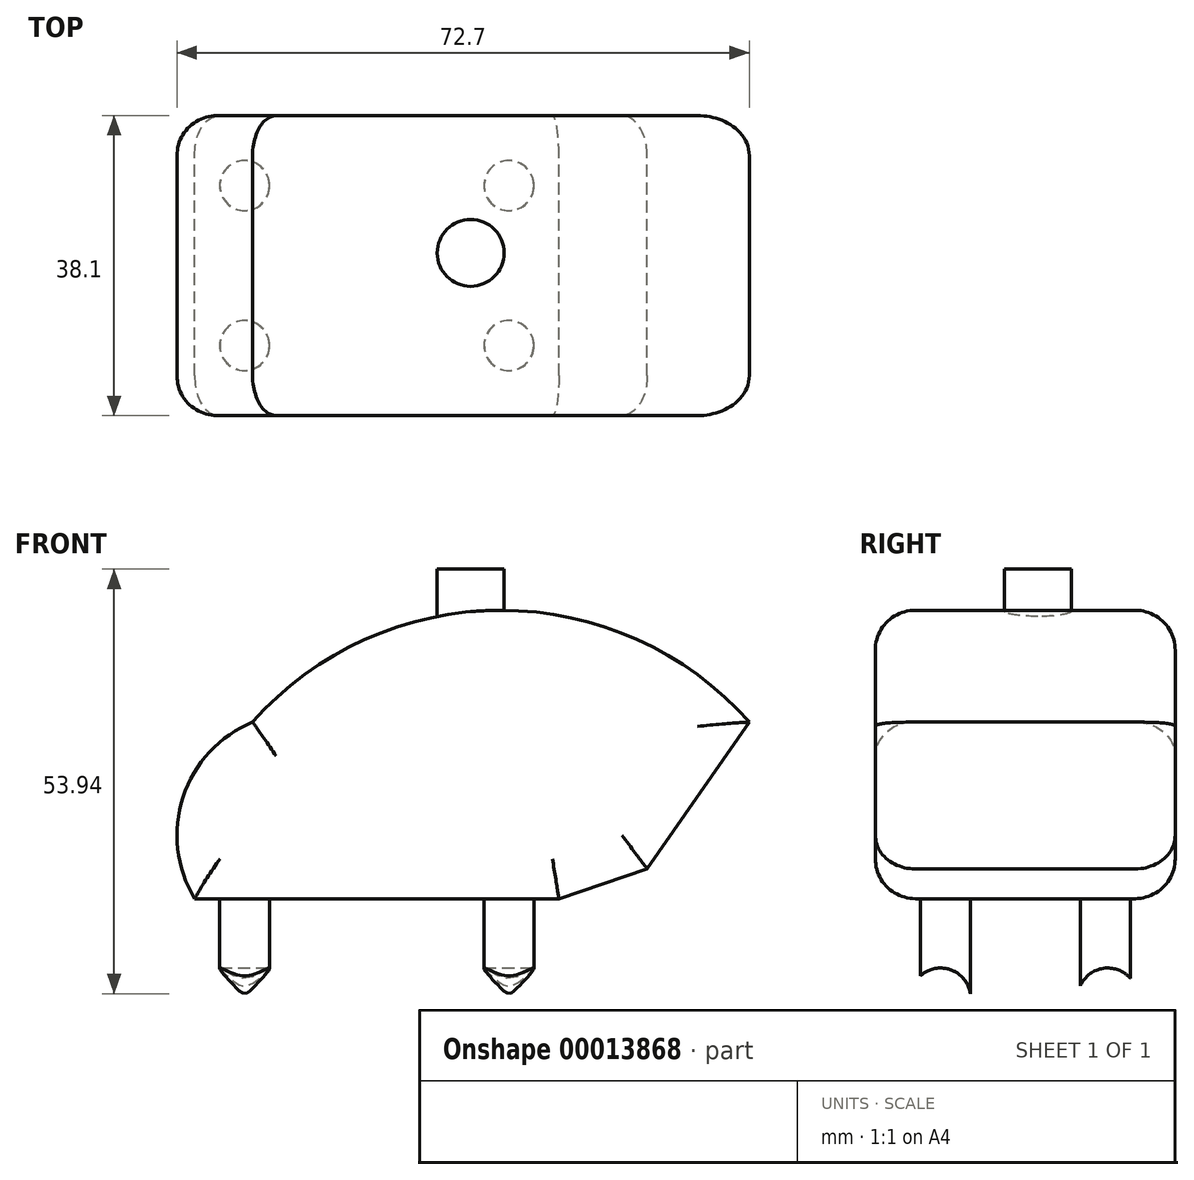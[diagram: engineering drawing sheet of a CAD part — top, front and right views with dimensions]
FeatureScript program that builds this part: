
annotation { "Feature Type Name" : "Feature", "Feature Type Description" : "" }
export const myFeature = defineFeature(function(context is Context, id is Id, definition is map)
    precondition{}
    {
        {
            var Q0;
            Q0=qCreatedBy(makeId("Front.planeOp"),FACE);
            var sketch = newSketch(context, id + "F0", { "sketchPlane" : qUnion([Q0])});
            skLineSegment(sketch, "E0", {"start": v(36.28, 0) * mm, "end": v(49.25, 18.67) * mm});
            skArc(sketch, "E1", {"start": v(49.25, 18.67) * mm, "mid": v(17.7, 32.86) * mm, "end": v(-13.85, 18.67) * mm});
            skArc(sketch, "E2", {"start": v(-13.85, 18.67) * mm, "mid": v(-22.68, 9.14) * mm, "end": v(-21.2, -3.77) * mm});
            skLineSegment(sketch, "E3", {"start": v(-21.2, -3.77) * mm, "end": v(25.06, -3.77) * mm});
            skLineSegment(sketch, "E4", {"start": v(25.06, -3.77) * mm, "end": v(36.28, 0) * mm});
            skSolve(sketch);
        }
        {
            var Q0;
            Q0 = qSketchRegion(id + "F0", true);
            extrude(context, id + "F1", {"entities" : qUnion([Q0]), "depth" : 38.1 * mm});
        }
        {
            var Q0;
            Q0=makeQuery(id+"F1.opExtrude","CAP_FACE",FACE,{"disambiguationData":[OSD([sQuery(id+"F0.wireOp",EDGE,"E0"),sQuery(id+"F0.wireOp",EDGE,"E1"),sQuery(id+"F0.wireOp",EDGE,"E2"),sQuery(id+"F0.wireOp",EDGE,"E3"),sQuery(id+"F0.wireOp",EDGE,"E4")])],"isStart":false});
            var Q1;
            Q1=makeQuery(id+"F1.opExtrude","CAP_FACE",FACE,{"disambiguationData":[OSD([sQuery(id+"F0.wireOp",EDGE,"E0"),sQuery(id+"F0.wireOp",EDGE,"E1"),sQuery(id+"F0.wireOp",EDGE,"E2"),sQuery(id+"F0.wireOp",EDGE,"E3"),sQuery(id+"F0.wireOp",EDGE,"E4")])],"isStart":true});
            fillet(context, id + "F2", {"entities" : qUnion([Q0, Q1]), "radius" : 5.08 * mm, "tangentPropagation" : true, "allowEdgeOverflow" : false});
        }
        {
            var Q0;
            Q0=makeQuery(id+"F1.opExtrude","SWEPT_FACE",FACE,{"disambiguationData":[OSD([sQuery(id+"F0.wireOp",EDGE,"E3")])]});
            var sketch = newSketch(context, id + "F3", { "sketchPlane" : qUnion([Q0])});
            skCircle(sketch, "E5", {"center": v(-14.86, 29.21) * mm, "radius": 3.18 * mm});
            skCircle(sketch, "E6", {"center": v(18.71, 29.21) * mm, "radius": 3.18 * mm});
            skCircle(sketch, "E7", {"center": v(18.71, 8.9) * mm, "radius": 3.18 * mm});
            skCircle(sketch, "E8", {"center": v(-14.86, 8.9) * mm, "radius": 3.18 * mm});
            skSolve(sketch);
        }
        {
            var Q0;
            Q0 = qSketchRegion(id + "F3", true);
            extrude(context, id + "F4", {"entities" : qUnion([Q0]), "operationType" : NewBodyOperationType.ADD, "depth" : 12.7 * mm});
        }
        {
            var Q0;
            Q0=qCreatedBy(makeId("Right.planeOp"),FACE);
            var sketch = newSketch(context, id + "F5", { "sketchPlane" : qUnion([Q0])});
            skCircle(sketch, "E9", {"center": v(-8.58, -16.39) * mm, "radius": 3.8 * mm});
            skCircle(sketch, "E10", {"center": v(-29.8, -16.39) * mm, "radius": 3.81 * mm});
            skSolve(sketch);
        }
        {
            var Q0;
            Q0 = qSketchRegion(id + "F5", true);
            extrude(context, id + "F6", {"entities" : qUnion([Q0]), "operationType" : NewBodyOperationType.REMOVE, "oppositeDirection" : true, "depth" : 127 * mm, "hasSecondDirection" : true, "secondDirectionOppositeDirection" : false, "secondDirectionDepth" : 127 * mm});
        }
        {
            var Q0;
            Q0=qCreatedBy(makeId("Top.planeOp"),FACE);
            var sketch = newSketch(context, id + "F7", { "sketchPlane" : qUnion([Q0])});
            skCircle(sketch, "E11", {"center": v(13.85, -17.44) * mm, "radius": 4.24 * mm});
            skSolve(sketch);
        }
        {
            var Q0;
            Q0 = qSketchRegion(id + "F7", true);
            extrude(context, id + "F8", {"entities" : qUnion([Q0]), "operationType" : NewBodyOperationType.ADD, "depth" : 38.1 * mm});
        }
    });
